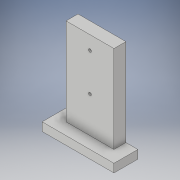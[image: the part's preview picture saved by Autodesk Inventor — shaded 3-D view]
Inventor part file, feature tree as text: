
AUTODESK INVENTOR PART (.ipt)
format: ipt  version: 2017 (Build 210142000, 142)  size: 122,368 bytes
history: native  units: in
note: dims shown in document units (in); Inventor stores cm internally (conversion verified against a paired STEP export)
features: extrude x2, sketch x2
ambient origin geometry x8: Origin, YZ Plane, XZ Plane, XY Plane, X Axis, Y Axis, Z Axis, Center Point
bodies: Solid1 (feature_tree)
feature tree (4):
  extrude  "Extrusion1"  Depth=1.575in
  extrude  "Extrusion3"  Depth=0.5in
  sketch  "Sketch1"  dims[d0=1.575in d1=0.6in]
  sketch  "Sketch3"  dims[d2=2.4in d3=0.122in d4=0.122in d5=0.57in d6=1.0in d7=1.0in d8=4.0in d9=0.5in d10=0.5in d11=0.35in d12=0.5in d13=0.0in d16=0.5in d17=0.0in]
